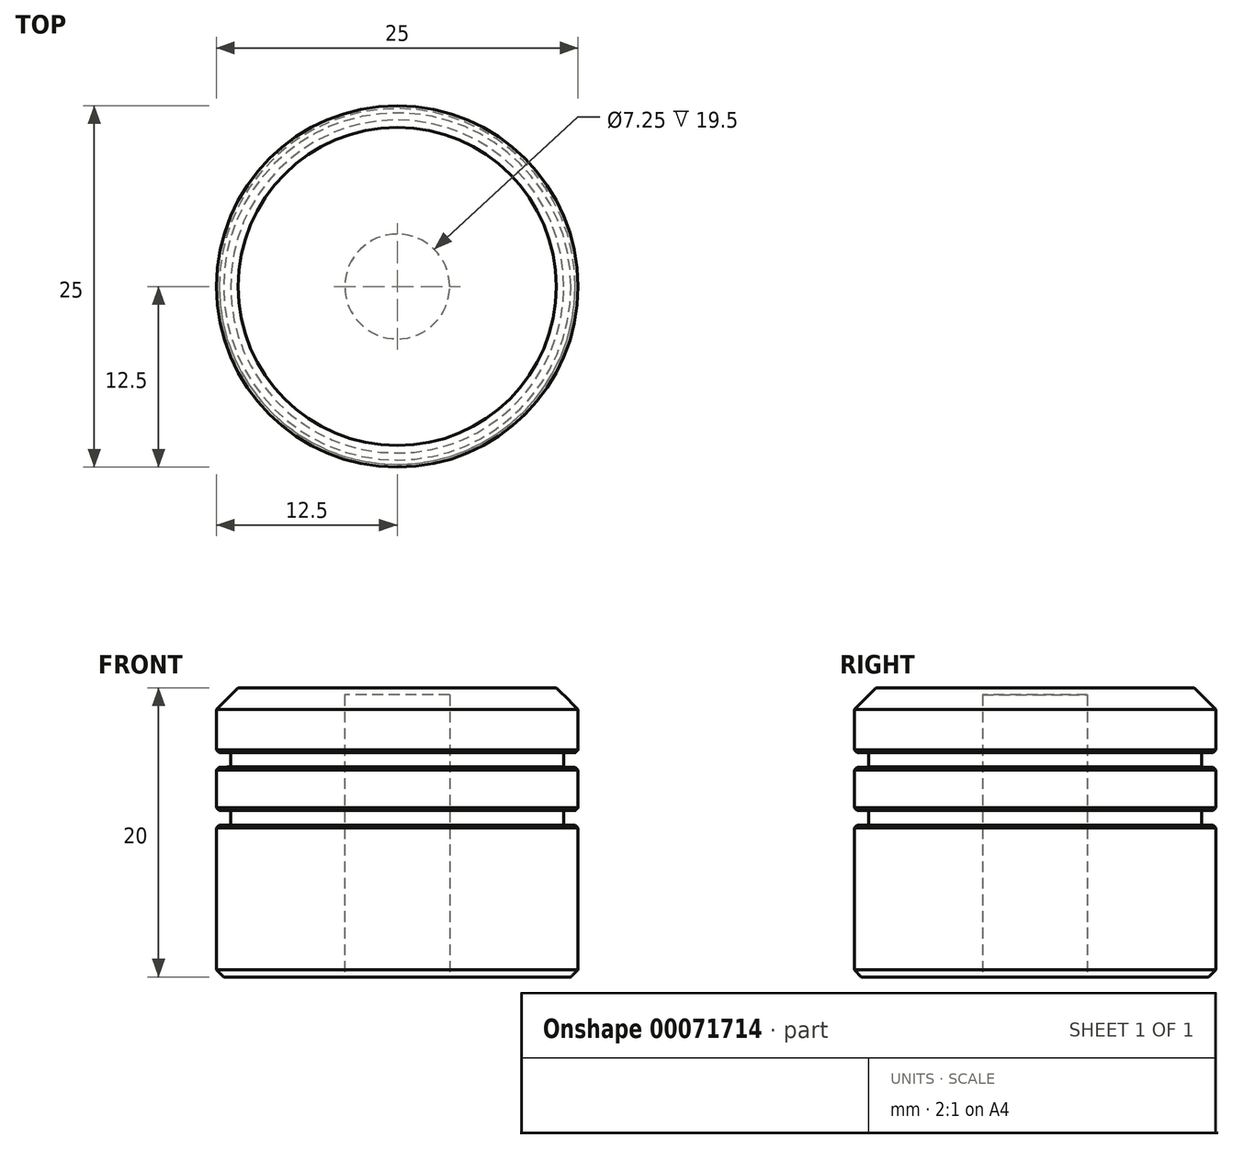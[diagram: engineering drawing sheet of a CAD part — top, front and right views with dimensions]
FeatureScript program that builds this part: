
annotation { "Feature Type Name" : "Feature", "Feature Type Description" : "" }
export const myFeature = defineFeature(function(context is Context, id is Id, definition is map)
    precondition{}
    {
        {
            var Q0;
            Q0=qCreatedBy(makeId("Top.planeOp"),FACE);
            var sketch = newSketch(context, id + "F0", { "sketchPlane" : qUnion([Q0])});
            skCircle(sketch, "E0", {"center": v(0, 0) * mm, "radius": 12.5 * mm});
            skSolve(sketch);
        }
        {
            var Q0;
            Q0 = qSketchRegion(id + "F0", true);
            extrude(context, id + "F1", {"entities" : qUnion([Q0]), "depth" : 20 * mm});
        }
        {
            var Q0;
            Q0=qCreatedBy(makeId("Top.planeOp"),FACE);
            var sketch = newSketch(context, id + "F2", { "sketchPlane" : qUnion([Q0])});
            skCircle(sketch, "E1", {"center": v(0, 0) * mm, "radius": 3.62 * mm});
            skSolve(sketch);
        }
        {
            var Q0;
            Q0 = qSketchRegion(id + "F2", true);
            extrude(context, id + "F3", {"entities" : qUnion([Q0]), "operationType" : NewBodyOperationType.REMOVE, "depth" : 19.5 * mm});
        }
        {
            var Q0;
            Q0=makeQuery(id+"F1.opExtrude","CAP_EDGE",EDGE,{"disambiguationData":[OSD([sQuery(id+"F0.wireOp",EDGE,"E0")])],"isStart":false});
            chamfer(context, id + "F4", {"entities" : qUnion([Q0]), "width" : 1.5 * mm, "tangentPropagation" : true});
        }
        {
            var Q0;
            Q0=makeQuery(id+"F1.opExtrude","CAP_EDGE",EDGE,{"disambiguationData":[OSD([sQuery(id+"F0.wireOp",EDGE,"E0")])],"isStart":true});
            var Q1;
            Q1=makeQuery(id+"F3.boolean.opBoolean","COPY",EDGE,{"derivedFrom":makeQuery(id+"F3.opExtrude","CAP_EDGE",EDGE,{"disambiguationData":[OSD([sQuery(id+"F2.wireOp",EDGE,"E1")])],"isStart":true})});
            chamfer(context, id + "F5", {"entities" : qUnion([Q0, Q1]), "width" : .5 * mm, "tangentPropagation" : true});
        }
        {
            var Q0;
            Q0=qCreatedBy(makeId("Right.planeOp"),FACE);
            var sketch = newSketch(context, id + "F6", { "sketchPlane" : qUnion([Q0])});
            skLineSegment(sketch, "E2", {"start": v(12.52, 15.5) * mm, "end": v(12.52, 14.5) * mm});
            skLineSegment(sketch, "E3", {"start": v(12.52, 11.5) * mm, "end": v(12.52, 10.5) * mm});
            skLineSegment(sketch, "E4", {"start": v(11.52, 15.5) * mm, "end": v(11.52, 14.52) * mm});
            skLineSegment(sketch, "E5", {"start": v(11.52, 14.52) * mm, "end": v(12.52, 14.5) * mm});
            skLineSegment(sketch, "E6", {"start": v(12.52, 15.5) * mm, "end": v(11.52, 15.5) * mm});
            skLineSegment(sketch, "E7", {"start": v(12.52, 11.5) * mm, "end": v(11.52, 11.5) * mm});
            skLineSegment(sketch, "E8", {"start": v(11.52, 10.5) * mm, "end": v(12.52, 10.5) * mm});
            skLineSegment(sketch, "E9", {"start": v(11.52, 11.5) * mm, "end": v(11.52, 10.5) * mm});
            skSolve(sketch);
        }
        {
            var Q0;
            Q0 = qSketchRegion(id + "F6", true);
            var Q1;
            Q1=makeQuery(id+"F1.opExtrude","SWEPT_FACE",FACE,{"disambiguationData":[OSD([sQuery(id+"F0.wireOp",EDGE,"E0")])]});
            revolve(context, id + "F7", {"operationType" : NewBodyOperationType.REMOVE, "entities" : qUnion([Q0]), "axis" : qUnion([Q1]), "revolveType" : RevolveType.FULL, "oppositeDirection" : true});
        }
        {
            var Q0;
            Q0=makeQuery(id+"F7.boolean.opBoolean","INTERSECT",EDGE,{"derivedFrom":[makeQuery(id+"F1.opExtrude","SWEPT_FACE",FACE,{"disambiguationData":[OSD([sQuery(id+"F0.wireOp",EDGE,"E0")])]}),makeQuery(id+"F7.opRevolve","SWEPT_FACE",FACE,{"disambiguationData":[OSD([sQuery(id+"F6.wireOp",EDGE,"E6")])]})]});
            var Q1;
            Q1=makeQuery(id+"F7.boolean.opBoolean","INTERSECT",EDGE,{"derivedFrom":[makeQuery(id+"F1.opExtrude","SWEPT_FACE",FACE,{"disambiguationData":[OSD([sQuery(id+"F0.wireOp",EDGE,"E0")])]}),makeQuery(id+"F7.opRevolve","SWEPT_FACE",FACE,{"disambiguationData":[OSD([sQuery(id+"F6.wireOp",EDGE,"E5")])]})]});
            var Q2;
            Q2=makeQuery(id+"F7.boolean.opBoolean","INTERSECT",EDGE,{"derivedFrom":[makeQuery(id+"F1.opExtrude","SWEPT_FACE",FACE,{"disambiguationData":[OSD([sQuery(id+"F0.wireOp",EDGE,"E0")])]}),makeQuery(id+"F7.opRevolve","SWEPT_FACE",FACE,{"disambiguationData":[OSD([sQuery(id+"F6.wireOp",EDGE,"E7")])]})]});
            var Q3;
            Q3=makeQuery(id+"F7.boolean.opBoolean","INTERSECT",EDGE,{"derivedFrom":[makeQuery(id+"F1.opExtrude","SWEPT_FACE",FACE,{"disambiguationData":[OSD([sQuery(id+"F0.wireOp",EDGE,"E0")])]}),makeQuery(id+"F7.opRevolve","SWEPT_FACE",FACE,{"disambiguationData":[OSD([sQuery(id+"F6.wireOp",EDGE,"E8")])]})]});
            chamfer(context, id + "F8", {"entities" : qUnion([Q0, Q1, Q2, Q3]), "width" : .2 * mm, "tangentPropagation" : true});
        }
    });
